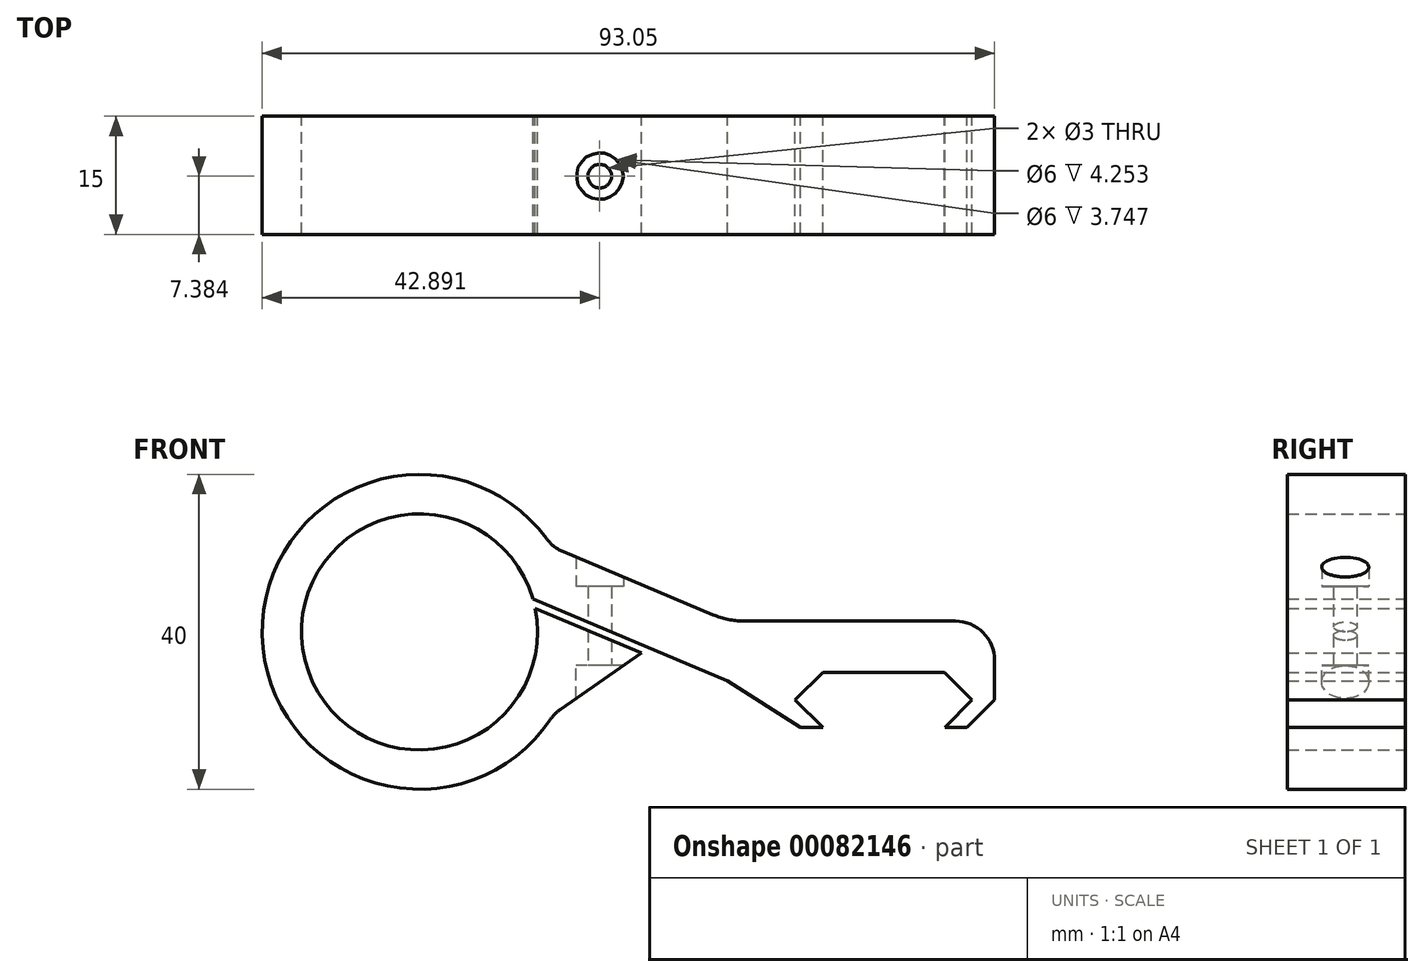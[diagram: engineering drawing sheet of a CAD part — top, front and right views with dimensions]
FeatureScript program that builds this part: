
annotation { "Feature Type Name" : "Feature", "Feature Type Description" : "" }
export const myFeature = defineFeature(function(context is Context, id is Id, definition is map)
    precondition{}
    {
        {
            var Q0;
            Q0=qCreatedBy(makeId("Front.planeOp"),FACE);
            var sketch = newSketch(context, id + "F0", { "sketchPlane" : qUnion([Q0])});
            skArc(sketch, "E0.0", {"start": v(-36.1, 15) * mm, "mid": v(-72.03, -1.74) * mm, "end": v(-32.96, 5) * mm});
            skLineSegment(sketch, "E1", {"start": v(-1.73, -7.89) * mm, "end": v(-5.23, -4.39) * mm});
            skLineSegment(sketch, "E2.MirrorCS", {"start": v(13.77, -7.89) * mm, "end": v(17.27, -4.39) * mm});
            skLineSegment(sketch, "E3.MirrorCS", {"start": v(16.6, -7.89) * mm, "end": v(20.1, -4.39) * mm});
            skLineSegment(sketch, "E4", {"start": v(20.1, 5.61) * mm, "end": v(20.1, -4.39) * mm});
            skLineSegment(sketch, "E5", {"start": v(-4.56, -7.89) * mm, "end": v(-1.73, -7.89) * mm});
            skLineSegment(sketch, "E6", {"start": v(13.77, -7.89) * mm, "end": v(16.6, -7.89) * mm});
            skLineSegment(sketch, "E7", {"start": v(-1.73, -0.89) * mm, "end": v(-5.23, -4.39) * mm});
            skLineSegment(sketch, "E8.MirrorCS", {"start": v(13.72, -0.89) * mm, "end": v(17.24, -4.44) * mm});
            skLineSegment(sketch, "E9", {"start": v(-1.73, -0.89) * mm, "end": v(6.02, -0.89) * mm});
            skLineSegment(sketch, "E10", {"start": v(13.72, -0.89) * mm, "end": v(6.02, -0.89) * mm});
            skLineSegment(sketch, "E11", {"start": v(20.1, 5.61) * mm, "end": v(-13.8, 5.63) * mm});
            skLineSegment(sketch, "E12", {"start": v(-13.8, -1.97) * mm, "end": v(-38.55, 8.45) * mm});
            skLineSegment(sketch, "E13.0", {"start": v(-13.8, 5.63) * mm, "end": v(-36.1, 15) * mm});
            skPoint(sketch, "E14.orphan", {"position": v(-8.06, 5.62) * mm});
            skLineSegment(sketch, "E15", {"start": v(-13.8, -1.97) * mm, "end": v(-4.56, -7.89) * mm});
            skArc(sketch, "E16.converted", {"start": v(-38.55, 8.45) * mm, "mid": v(-67.5, 0.63) * mm, "end": v(-38.25, 7.24) * mm});
            skLineSegment(sketch, "E17.0", {"start": v(-24.76, 1.56) * mm, "end": v(-38.25, 7.24) * mm});
            skLineSegment(sketch, "E18", {"start": v(-35.88, -6.19) * mm, "end": v(-24.76, 1.56) * mm});
            skSolve(sketch);
        }
        {
            var Q0;
            Q0=makeQuery(id+"F0.imprint","IMPRINT",FACE,{"disambiguationData":[TD([[makeQuery(id+"F0.imprint","IMPRINT",EDGE,{"derivedFrom":sQuery(id+"F0.wireOp",EDGE,"E1")}),1.0]])]});
            var Q1;
            {var subQ3=sQuery(id+"F0.wireOp",EDGE,"E18");Q1=makeQuery(id+"F0.imprint","IMPRINT",FACE,{"disambiguationData":[TD([[makeQuery(id+"F0.imprint","IMPRINT",EDGE,{"derivedFrom":subQ3}),1.0]])]});}
            extrude(context, id + "F1", {"entities" : qUnion([Q0, Q1]), "depth" : 15 * mm});
        }
        {
            var Q0;
            Q0=qCreatedBy(makeId("Top.planeOp"),FACE);
            var sketch = newSketch(context, id + "F2", { "sketchPlane" : qUnion([Q0])});
            skLineSegment(sketch, "E19", {"start": v(-32.06, 0) * mm, "end": v(-32.06, -14.93) * mm});
            skCircle(sketch, "E20", {"center": v(-30.06, -7.62) * mm, "radius": 2 * mm});
            skSolve(sketch);
        }
        {
            var Q0;
            Q0=sQuery(id+"F2.wireOp",VERTEX,"E20.center");
            var Q1;
            Q1=makeQuery(id+"F1.opExtrude","SWEPT_BODY",BODY,{"disambiguationData":[OSD([sQuery(id+"F0.wireOp",EDGE,"E0.0"),sQuery(id+"F0.wireOp",EDGE,"E1"),sQuery(id+"F0.wireOp",EDGE,"E2.MirrorCS"),sQuery(id+"F0.wireOp",EDGE,"E3.MirrorCS"),sQuery(id+"F0.wireOp",EDGE,"E4"),sQuery(id+"F0.wireOp",EDGE,"E5"),sQuery(id+"F0.wireOp",EDGE,"E6"),sQuery(id+"F0.wireOp",EDGE,"E7"),sQuery(id+"F0.wireOp",EDGE,"E8.MirrorCS"),sQuery(id+"F0.wireOp",EDGE,"E9"),sQuery(id+"F0.wireOp",EDGE,"E10"),sQuery(id+"F0.wireOp",EDGE,"E11"),sQuery(id+"F0.wireOp",EDGE,"8fb95515-4d3a-4773-8a77-53325fa898fe.filletArc"),sQuery(id+"F0.wireOp",EDGE,"E12"),sQuery(id+"F0.wireOp",EDGE,"E13.0"),sQuery(id+"F0.wireOp",EDGE,"E15"),sQuery(id+"F0.wireOp",EDGE,"E16.converted"),sQuery(id+"F0.wireOp",EDGE,"E17.0"),sQuery(id+"F0.wireOp",EDGE,"E18")])]});
            hole(context, id + "F3", {"style" : HoleStyle.SIMPLE, "endStyle" : HoleEndStyle.THROUGH, "oppositeDirection" : true, "holeDiameter" : 3 * mm, "startFromSketch" : true, "locations" : qUnion([Q0]), "scope" : qUnion([Q1]), "isTappedThrough" : true});
        }
        {
            var Q0;
            Q0=sQuery(id+"F2.wireOp",VERTEX,"E20.center");
            var Q1;
            Q1=makeQuery(id+"F1.opExtrude","SWEPT_BODY",BODY,{"disambiguationData":[OSD([sQuery(id+"F0.wireOp",EDGE,"E0.0"),sQuery(id+"F0.wireOp",EDGE,"E1"),sQuery(id+"F0.wireOp",EDGE,"E2.MirrorCS"),sQuery(id+"F0.wireOp",EDGE,"E3.MirrorCS"),sQuery(id+"F0.wireOp",EDGE,"E4"),sQuery(id+"F0.wireOp",EDGE,"E5"),sQuery(id+"F0.wireOp",EDGE,"E6"),sQuery(id+"F0.wireOp",EDGE,"E7"),sQuery(id+"F0.wireOp",EDGE,"E8.MirrorCS"),sQuery(id+"F0.wireOp",EDGE,"E9"),sQuery(id+"F0.wireOp",EDGE,"E10"),sQuery(id+"F0.wireOp",EDGE,"E11"),sQuery(id+"F0.wireOp",EDGE,"8fb95515-4d3a-4773-8a77-53325fa898fe.filletArc"),sQuery(id+"F0.wireOp",EDGE,"E12"),sQuery(id+"F0.wireOp",EDGE,"E13.0"),sQuery(id+"F0.wireOp",EDGE,"E15"),sQuery(id+"F0.wireOp",EDGE,"E16.converted"),sQuery(id+"F0.wireOp",EDGE,"E17.0"),sQuery(id+"F0.wireOp",EDGE,"E18")])]});
            hole(context, id + "F4", {"style" : HoleStyle.SIMPLE, "endStyle" : HoleEndStyle.BLIND, "holeDiameter" : 3 * mm, "holeDepth" : 40 * mm, "startFromSketch" : true, "locations" : qUnion([Q0]), "scope" : qUnion([Q1])});
        }
        {
            var Q0;
            Q0=qCreatedBy(makeId("Top.planeOp"),FACE);
            var sketch = newSketch(context, id + "F5", { "sketchPlane" : qUnion([Q0])});
            skCircle(sketch, "E21", {"center": v(-30.06, -7.62) * mm, "radius": 1.5 * mm});
            skCircle(sketch, "E22.0", {"center": v(-30.06, -7.62) * mm, "radius": 3 * mm});
            skSolve(sketch);
        }
        {
            var Q0;
            Q0 = qSketchRegion(id + "F5", true);
            extrude(context, id + "F6", {"entities" : qUnion([Q0]), "operationType" : NewBodyOperationType.REMOVE, "oppositeDirection" : true, "depth" : 25 * mm});
        }
        {
            var Q0;
            Q0=qCreatedBy(makeId("Top.planeOp"),FACE);
            cPlane(context, id + "F7", {"entities" : qUnion([Q0]), "cplaneType" : CPlaneType.OFFSET, "offset" : 10 * mm, "width" : 150 * mm, "height" : 150 * mm});
        }
        {
            var Q0;
            Q0=qCreatedBy(id+"F7.planeOp",FACE);
            var sketch = newSketch(context, id + "F8", { "sketchPlane" : qUnion([Q0])});
            skCircle(sketch, "E23.0", {"center": v(-30.06, -7.62) * mm, "radius": 3 * mm});
            skSolve(sketch);
        }
        {
            var Q0;
            Q0=makeQuery(id+"F1.opExtrude","SWEPT_EDGE",EDGE,{"disambiguationData":[OSD([sQuery(id+"F0.wireOp",EDGE,"E11"),sQuery(id+"F0.wireOp",EDGE,"E13.0")])]});
            fillet(context, id + "F9", {"entities" : qUnion([Q0]), "radius" : 10 * mm, "tangentPropagation" : true, "allowEdgeOverflow" : false});
        }
        {
            var Q0;
            Q0=makeQuery(id+"F1.opExtrude","SWEPT_EDGE",EDGE,{"disambiguationData":[OSD([sQuery(id+"F0.wireOp",EDGE,"E4"),sQuery(id+"F0.wireOp",EDGE,"E11")])]});
            fillet(context, id + "F10", {"entities" : qUnion([Q0]), "radius" : 5 * mm, "tangentPropagation" : true, "allowEdgeOverflow" : false});
        }
        {
            var Q0;
            Q0=makeQuery(id+"F1.opExtrude","SWEPT_EDGE",EDGE,{"disambiguationData":[OSD([sQuery(id+"F0.wireOp",EDGE,"E0.0"),sQuery(id+"F0.wireOp",EDGE,"E13.0")])]});
            fillet(context, id + "F11", {"entities" : qUnion([Q0]), "radius" : 5 * mm, "tangentPropagation" : true, "allowEdgeOverflow" : false});
        }
        {
            var Q0;
            Q0=makeQuery(id+"F1.opExtrude","SWEPT_EDGE",EDGE,{"disambiguationData":[OSD([sQuery(id+"F0.wireOp",EDGE,"E0.0"),sQuery(id+"F0.wireOp",EDGE,"E18")])]});
            fillet(context, id + "F12", {"entities" : qUnion([Q0]), "radius" : 5 * mm, "tangentPropagation" : true, "allowEdgeOverflow" : false});
        }
        {
            var Q0;
            Q0 = qSketchRegion(id + "F8", true);
            extrude(context, id + "F13", {"entities" : qUnion([Q0]), "operationType" : NewBodyOperationType.REMOVE, "depth" : 25 * mm});
        }
    });
